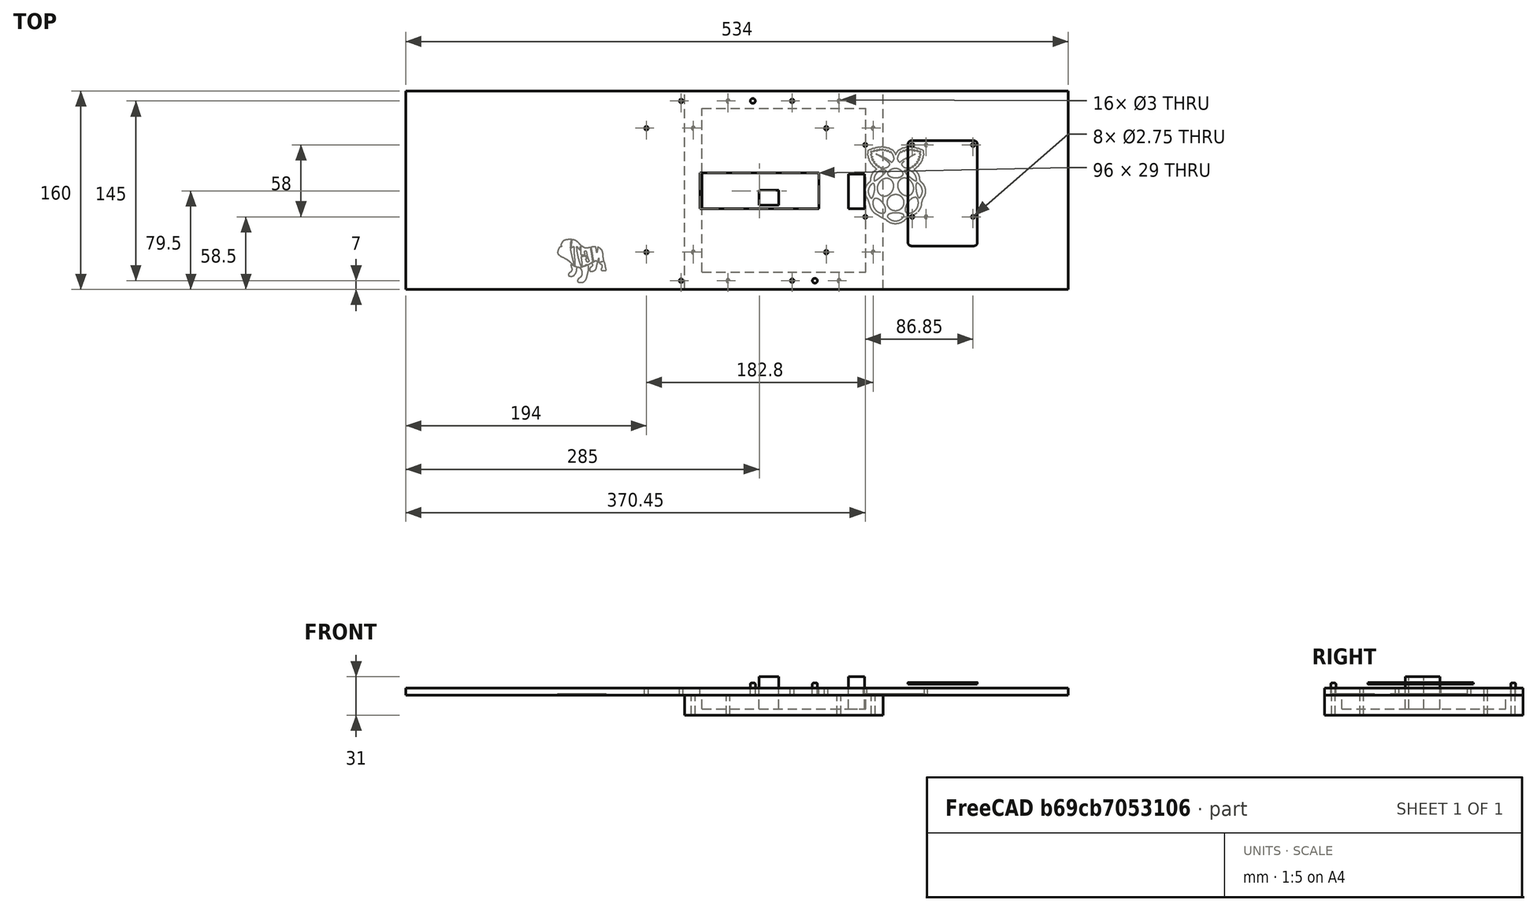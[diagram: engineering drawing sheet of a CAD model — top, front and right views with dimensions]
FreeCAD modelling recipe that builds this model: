
FCSTD DOCUMENT  (FreeCAD 0.19R)
Label: BigLEDWindowArray
License: All rights reserved
LicenseURL: http://en.wikipedia.org/wiki/All_rights_reserved
objects: Part::Feature×34, Part::Cylinder×26, Part::Extrusion×15, Part::Cut×10, Part::Box×9, Part::MultiFuse×9, Part::Fillet×3, Part::FeaturePython×2, TechDraw::DrawSVGTemplate×1, TechDraw::DrawViewPart×1, TechDraw::DrawPage×1
note: 108 computed .brp shape members not serialized (recipe doc carries the construction recipe); baked Part::Feature solids carry a one-line shape summary decoded from their .brp

FEATURE [Part::Box] Box  label="Cube"
  AttacherType = Attacher::AttachEngine3D
  Height = 16
  Length = 160
  Width = 160
FEATURE [Part::Cylinder] Cylinder
  Angle = 360
  AttacherType = Attacher::AttachEngine3D
  Height = 16
  Placement = pos=(35,7,0) rot=(0,0,1;0rad)
  Radius = 1.5
FEATURE [Part::Cylinder] Cylinder001
  Angle = 360
  AttacherType = Attacher::AttachEngine3D
  Height = 16
  Placement = pos=(124.5,7,0) rot=(0,0,1;0rad)
  Radius = 1.5
FEATURE [Part::Cylinder] Cylinder002
  Angle = 360
  AttacherType = Attacher::AttachEngine3D
  Height = 16
  Placement = pos=(35,152,0) rot=(0,0,1;0rad)
  Radius = 1.5
FEATURE [Part::Cylinder] Cylinder003
  Angle = 360
  AttacherType = Attacher::AttachEngine3D
  Height = 16
  Placement = pos=(124.5,152,0) rot=(0,0,1;0rad)
  Radius = 1.5
FEATURE [Part::Cylinder] Cylinder004
  Angle = 360
  AttacherType = Attacher::AttachEngine3D
  Height = 16
  Placement = pos=(7,30,0) rot=(0,0,1;0rad)
  Radius = 1.5
FEATURE [Part::Cylinder] Cylinder005
  Angle = 360
  AttacherType = Attacher::AttachEngine3D
  Height = 16
  Placement = pos=(7,130,0) rot=(0,0,1;0rad)
  Radius = 1.5
FEATURE [Part::Cylinder] Cylinder006
  Angle = 360
  AttacherType = Attacher::AttachEngine3D
  Height = 16
  Placement = pos=(152,30,0) rot=(0,0,1;0rad)
  Radius = 1.5
FEATURE [Part::Cylinder] Cylinder007
  Angle = 360
  AttacherType = Attacher::AttachEngine3D
  Height = 16
  Placement = pos=(152,130,0) rot=(0,0,1;0rad)
  Radius = 1.5
FEATURE [Part::MultiFuse] Fusion  label="Anchor Holes"
  Shapes = -> [Cylinder007,Cylinder,Cylinder001,Cylinder002,Cylinder003,Cylinder004,Cylinder005,Cylinder006]
FEATURE [Part::Box] Box001  label="Cube001"
  AttacherType = Attacher::AttachEngine3D
  Height = 11
  Length = 132
  Placement = pos=(14,14,5) rot=(0,0,1;0rad)
  Width = 132
FEATURE [Part::Cut] Cut
  Base = -> Box
  Tool = -> Box001
FEATURE [Part::Box] Box002  label="Cube002"
  AttacherType = Attacher::AttachEngine3D
  Height = 26
  Length = 16
  Placement = pos=(60,68,5) rot=(0,0,1;0rad)
  Width = 12
FEATURE [Part::Box] Box003  label="Cube003"
  AttacherType = Attacher::AttachEngine3D
  Height = 26
  Length = 13
  Placement = pos=(132,65,5) rot=(0,0,1;0rad)
  Width = 28
FEATURE [Part::Cut] Cut001
  Base = -> Cut
  Tool = -> Fusion
FEATURE [Part::MultiFuse] Fusion001
  Shapes = -> [Cut001,Box002,Box003]
FEATURE [Part::Cylinder] Cylinder008
  Angle = 360
  AttacherType = Attacher::AttachEngine3D
  Height = 10
  Placement = pos=(105,7,16) rot=(0,0,1;0rad)
  Radius = 2
FEATURE [Part::Cylinder] Cylinder009
  Angle = 360
  AttacherType = Attacher::AttachEngine3D
  Height = 10
  Placement = pos=(55,152,16) rot=(0,0,1;0rad)
  Radius = 2
FEATURE [Part::Fillet] Fillet
  Base = -> Cylinder009
  Edges = 1 edges r=1: [Edge1]
FEATURE [Part::Fillet] Fillet001
  Base = -> Cylinder008
  Edges = 1 edges r=1: [Edge1]
FEATURE [Part::MultiFuse] Fusion002  label="LED Array"
  Placement = pos=(224.8,0,-16) rot=(0,0,1;0rad)
  Shapes = -> [Fusion001,Fillet,Fillet001]
FEATURE [Part::Box] Box004  label="Plexiglass Base"
  AttacherType = Attacher::AttachEngine3D
  Height = 6
  Length = 609.6
  Width = 160
FEATURE [Part::Box] Box005  label="Main Cabling Hole"
  AttacherType = Attacher::AttachEngine3D
  Height = 6
  Length = 96
  Placement = pos=(274.8,65,0) rot=(0,0,1;0rad)
  Width = 29
FEATURE [Part::Box] Box006  label="Cube004"
  AttacherType = Attacher::AttachEngine3D
  Height = 1.4
  Length = 56
  Placement = pos=(0,0,9) rot=(0,0,1;0rad)
  Width = 85
FEATURE [Part::Fillet] Fillet002  label="Pi Base Board"
  Base = -> Box006
  Edges = 4 edges r=3: [Edge1,Edge3,Edge5,Edge7]
FEATURE [Part::Cylinder] Cylinder010
  Angle = 360
  AttacherType = Attacher::AttachEngine3D
  Height = 1.4
  Placement = pos=(3.5,81.5,9) rot=(0,0,1;0rad)
  Radius = 1.375
FEATURE [Part::Cylinder] Cylinder011
  Angle = 360
  AttacherType = Attacher::AttachEngine3D
  Height = 1.4
  Placement = pos=(52.5,81.5,9) rot=(0,0,1;0rad)
  Radius = 1.375
FEATURE [Part::Cylinder] Cylinder012
  Angle = 360
  AttacherType = Attacher::AttachEngine3D
  Height = 1.4
  Placement = pos=(52.5,23.5,9) rot=(0,0,1;0rad)
  Radius = 1.375
FEATURE [Part::Cylinder] Cylinder013
  Angle = 360
  AttacherType = Attacher::AttachEngine3D
  Height = 1.4
  Placement = pos=(3.5,23.5,9) rot=(0,0,1;0rad)
  Radius = 1.375
FEATURE [Part::MultiFuse] Fusion003  label="Pi Board Holes"
  Shapes = -> [Cylinder010,Cylinder011,Cylinder012,Cylinder013]
FEATURE [Part::Cut] Cut002  label="Pi base Board"
  Base = -> Fillet002
  Placement = pos=(404.8,35,0) rot=(0,0,1;0rad)
  Tool = -> Fusion003
FEATURE [Part::Cut] Cut003
  Base = -> Box004
  Tool = -> Box005
FEATURE [Part::Cylinder] Cylinder014
  Angle = 360
  AttacherType = Attacher::AttachEngine3D
  Height = 16
  Placement = pos=(35,152,0) rot=(0,0,1;0rad)
  Radius = 1.5
FEATURE [Part::Cylinder] Cylinder015
  Angle = 360
  AttacherType = Attacher::AttachEngine3D
  Height = 16
  Placement = pos=(152,130,0) rot=(0,0,1;0rad)
  Radius = 1.5
FEATURE [Part::Cylinder] Cylinder016
  Angle = 360
  AttacherType = Attacher::AttachEngine3D
  Height = 16
  Placement = pos=(124.5,7,0) rot=(0,0,1;0rad)
  Radius = 1.5
FEATURE [Part::Cylinder] Cylinder017
  Angle = 360
  AttacherType = Attacher::AttachEngine3D
  Height = 16
  Placement = pos=(7,30,0) rot=(0,0,1;0rad)
  Radius = 1.5
FEATURE [Part::Cylinder] Cylinder018
  Angle = 360
  AttacherType = Attacher::AttachEngine3D
  Height = 16
  Placement = pos=(7,130,0) rot=(0,0,1;0rad)
  Radius = 1.5
FEATURE [Part::Cylinder] Cylinder019
  Angle = 360
  AttacherType = Attacher::AttachEngine3D
  Height = 16
  Placement = pos=(152,30,0) rot=(0,0,1;0rad)
  Radius = 1.5
FEATURE [Part::Cylinder] Cylinder020
  Angle = 360
  AttacherType = Attacher::AttachEngine3D
  Height = 16
  Placement = pos=(124.5,152,0) rot=(0,0,1;0rad)
  Radius = 1.5
FEATURE [Part::Cylinder] Cylinder021
  Angle = 360
  AttacherType = Attacher::AttachEngine3D
  Height = 16
  Placement = pos=(35,7,0) rot=(0,0,1;0rad)
  Radius = 1.5
FEATURE [Part::MultiFuse] Fusion004  label="Anchor Holes001"
  Placement = pos=(224.8,0,-6) rot=(0,0,1;0rad)
  Shapes = -> [Cylinder015,Cylinder021,Cylinder016,Cylinder014,Cylinder020,Cylinder017,Cylinder018,Cylinder019]
FEATURE [Part::Cut] Cut004
  Base = -> Cut003
  Tool = -> Fusion004
FEATURE [Part::Cylinder] Cylinder022
  Angle = 360
  AttacherType = Attacher::AttachEngine3D
  Height = 6
  Placement = pos=(3.5,81.5,9) rot=(0,0,1;0rad)
  Radius = 1.375
FEATURE [Part::Cylinder] Cylinder023
  Angle = 360
  AttacherType = Attacher::AttachEngine3D
  Height = 6
  Placement = pos=(52.5,81.5,9) rot=(0,0,1;0rad)
  Radius = 1.375
FEATURE [Part::Cylinder] Cylinder024
  Angle = 360
  AttacherType = Attacher::AttachEngine3D
  Height = 6
  Placement = pos=(52.5,23.5,9) rot=(0,0,1;0rad)
  Radius = 1.375
FEATURE [Part::Cylinder] Cylinder025
  Angle = 360
  AttacherType = Attacher::AttachEngine3D
  Height = 6
  Placement = pos=(3.5,23.5,9) rot=(0,0,1;0rad)
  Radius = 1.375
FEATURE [Part::MultiFuse] Fusion005  label="Pi Board Holes001"
  Placement = pos=(404.75,35,-9) rot=(0,0,1;0rad)
  Shapes = -> [Cylinder022,Cylinder023,Cylinder024,Cylinder025]
FEATURE [Part::Cut] Cut005
  Base = -> Cut004
  Tool = -> Fusion005
FEATURE [Part::Feature] path94001
  shape: bbox 33.87 x 16.22 x 2e-07 mm, 1 faces, 0 solids (baked)
FEATURE [Part::Feature] path94003
  shape: bbox 26.79 x 32.02 x 2e-07 mm, 1 faces, 0 solids (baked)
FEATURE [Part::Feature] path94011
  shape: bbox 31.87 x 18.53 x 2e-07 mm, 1 faces, 0 solids (baked)
FEATURE [Part::Feature] path94013
  shape: bbox 47.72 x 38.86 x 2e-07 mm, 1 faces, 0 solids (baked)
FEATURE [Part::Feature] path94012
  shape: bbox 47.88 x 38.81 x 2e-07 mm, 1 faces, 0 solids (baked)
FEATURE [Part::Feature] path94009
  shape: bbox 25.13 x 21.74 x 2e-07 mm, 1 faces, 0 solids (baked)
FEATURE [Part::Feature] path94010
  shape: bbox 24.8 x 21.99 x 2e-07 mm, 1 faces, 0 solids (baked)
FEATURE [Part::Feature] path94007
  shape: bbox 33.34 x 35.47 x 2e-07 mm, 1 faces, 0 solids (baked)
FEATURE [Part::Feature] path94005
  shape: bbox 13.29 x 29.98 x 2e-07 mm, 1 faces, 0 solids (baked)
FEATURE [Part::Feature] path94004
  shape: bbox 34.84 x 32.78 x 2e-07 mm, 1 faces, 0 solids (baked)
FEATURE [Part::Feature] path94006
  shape: bbox 13.93 x 30.32 x 2e-07 mm, 1 faces, 0 solids (baked)
FEATURE [Part::Feature] path94008
  shape: bbox 32.64 x 35.5 x 2e-07 mm, 1 faces, 0 solids (baked)
FEATURE [Part::Feature] path94
  shape: bbox 121.7 x 156.1 x 2e-07 mm, 1 faces, 0 solids (baked)
FEATURE [Part::Feature] path94002
  shape: bbox 26 x 29.63 x 2e-07 mm, 1 faces, 0 solids (baked)
FEATURE [Part::Extrusion] Extrude001
  Base = -> path94001
  Dir = (0,0,1)
  DirMode = 0
  FaceMakerClass = Part::FaceMakerBullseye
  LengthFwd = 1
  LengthRev = 0
  Solid = false
  Symmetric = false
FEATURE [Part::Extrusion] Extrude
  Base = -> path94
  Dir = (0,0,1)
  DirMode = 0
  FaceMakerClass = Part::FaceMakerBullseye
  LengthFwd = 1
  LengthRev = 0
  Solid = false
  Symmetric = false
FEATURE [Part::Extrusion] Extrude012
  Base = -> path94012
  Dir = (0,0,1)
  DirMode = 0
  FaceMakerClass = Part::FaceMakerBullseye
  LengthFwd = 1
  LengthRev = 0
  Solid = false
  Symmetric = false
FEATURE [Part::Extrusion] Extrude013
  Base = -> path94013
  Dir = (0,0,1)
  DirMode = 0
  FaceMakerClass = Part::FaceMakerBullseye
  LengthFwd = 1
  LengthRev = 0
  Solid = false
  Symmetric = false
FEATURE [Part::Extrusion] Extrude007
  Base = -> path94007
  Dir = (0,0,1)
  DirMode = 0
  FaceMakerClass = Part::FaceMakerBullseye
  LengthFwd = 1
  LengthRev = 0
  Solid = false
  Symmetric = false
FEATURE [Part::Extrusion] Extrude008
  Base = -> path94008
  Dir = (0,0,1)
  DirMode = 0
  FaceMakerClass = Part::FaceMakerBullseye
  LengthFwd = 1
  LengthRev = 0
  Solid = false
  Symmetric = false
FEATURE [Part::Extrusion] Extrude009
  Base = -> path94009
  Dir = (0,0,1)
  DirMode = 0
  FaceMakerClass = Part::FaceMakerBullseye
  LengthFwd = 1
  LengthRev = 0
  Solid = false
  Symmetric = false
FEATURE [Part::Extrusion] Extrude010
  Base = -> path94010
  Dir = (0,0,1)
  DirMode = 0
  FaceMakerClass = Part::FaceMakerBullseye
  LengthFwd = 1
  LengthRev = 0
  Solid = false
  Symmetric = false
FEATURE [Part::Extrusion] Extrude011
  Base = -> path94011
  Dir = (0,0,1)
  DirMode = 0
  FaceMakerClass = Part::FaceMakerBullseye
  LengthFwd = 1
  LengthRev = 0
  Solid = false
  Symmetric = false
FEATURE [Part::Extrusion] Extrude002
  Base = -> path94002
  Dir = (0,0,1)
  DirMode = 0
  FaceMakerClass = Part::FaceMakerBullseye
  LengthFwd = 1
  LengthRev = 0
  Solid = false
  Symmetric = false
FEATURE [Part::Extrusion] Extrude003
  Base = -> path94003
  Dir = (0,0,1)
  DirMode = 0
  FaceMakerClass = Part::FaceMakerBullseye
  LengthFwd = 1
  LengthRev = 0
  Solid = false
  Symmetric = false
FEATURE [Part::Extrusion] Extrude004
  Base = -> path94004
  Dir = (0,0,1)
  DirMode = 0
  FaceMakerClass = Part::FaceMakerBullseye
  LengthFwd = 1
  LengthRev = 0
  Solid = false
  Symmetric = false
FEATURE [Part::Extrusion] Extrude005
  Base = -> path94005
  Dir = (0,0,1)
  DirMode = 0
  FaceMakerClass = Part::FaceMakerBullseye
  LengthFwd = 1
  LengthRev = 0
  Solid = false
  Symmetric = false
FEATURE [Part::Extrusion] Extrude006
  Base = -> path94006
  Dir = (0,0,1)
  DirMode = 0
  FaceMakerClass = Part::FaceMakerBullseye
  LengthFwd = 1
  LengthRev = 0
  Solid = false
  Symmetric = false
FEATURE [Part::MultiFuse] Fusion006
  Shapes = -> [Extrude001,Extrude002,Extrude003,Extrude004,Extrude005,Extrude006,Extrude007,Extrude008,Extrude009,Extrude010,Extrude011,Extrude012,Extrude013]
FEATURE [Part::Cut] Cut006  label="Pi Logo Base"
  Base = -> Extrude
  Tool = -> Fusion006
FEATURE [Part::FeaturePython] Clone  label="Pi Logo Scaled"  # Draft clone (typed FeaturePython)
  AttacherType = Attacher::AttachEngine3D
  Fuse = false
  Objects = -> [Cut006]
  Placement = pos=(408,115,0) rot=(0,0,1;0rad)
  Scale = (0.4,0.4,1)
FEATURE [Part::Cut] Cut007  label="Cut008"
  Base = -> Cut005
  Tool = -> Clone
FEATURE [Part::Feature] path821
  shape: bbox 45.55 x 68.49 x 2e-07 mm, 1 faces, 0 solids (baked)
FEATURE [Part::Feature] path821012
  shape: bbox 68.21 x 106 x 2e-07 mm, 1 faces, 0 solids (baked)
FEATURE [Part::Feature] path821018
  shape: bbox 52.44 x 63.16 x 2e-07 mm, 1 faces, 0 solids (baked)
FEATURE [Part::Feature] path821015
  shape: bbox 6.997 x 23.23 x 2e-07 mm, 1 faces, 0 solids (baked)
FEATURE [Part::Feature] path821019
  shape: bbox 51.27 x 62.42 x 2e-07 mm, 1 faces, 0 solids (baked)
FEATURE [Part::Feature] path821002
  shape: bbox 35.55 x 51.16 x 2e-07 mm, 1 faces, 0 solids (baked)
FEATURE [Part::Feature] path821009
  shape: bbox 42.61 x 110.8 x 2e-07 mm, 1 faces, 0 solids (baked)
FEATURE [Part::Feature] path821014
  shape: bbox 7.359 x 24.27 x 2e-07 mm, 1 faces, 0 solids (baked)
FEATURE [Part::Feature] path821017
  shape: bbox 6.224 x 14.06 x 2e-07 mm, 1 faces, 0 solids (baked)
FEATURE [Part::Feature] path821011
  shape: bbox 48.65 x 80.12 x 2e-07 mm, 1 faces, 0 solids (baked)
FEATURE [Part::Feature] path821007
  shape: bbox 26.33 x 36.96 x 2e-07 mm, 1 faces, 0 solids (baked)
FEATURE [Part::Feature] path821003
  shape: bbox 35.13 x 49.65 x 2e-07 mm, 1 faces, 0 solids (baked)
FEATURE [Part::Feature] path821008
  shape: bbox 43.59 x 111.6 x 2e-07 mm, 1 faces, 0 solids (baked)
FEATURE [Part::Feature] path821001
  shape: bbox 44.63 x 68.06 x 2e-07 mm, 1 faces, 0 solids (baked)
FEATURE [Part::Feature] path821013
  shape: bbox 67.42 x 105.1 x 2e-07 mm, 1 faces, 0 solids (baked)
FEATURE [Part::Feature] path821010
  shape: bbox 49.55 x 81.35 x 2e-07 mm, 1 faces, 0 solids (baked)
FEATURE [Part::Feature] path821004
  shape: bbox 33.13 x 41.25 x 2e-07 mm, 1 faces, 0 solids (baked)
FEATURE [Part::Feature] path821005
  shape: bbox 32.33 x 40.59 x 2e-07 mm, 1 faces, 0 solids (baked)
FEATURE [Part::Feature] path821006
  shape: bbox 26.59 x 37.55 x 2e-07 mm, 1 faces, 0 solids (baked)
FEATURE [Part::Feature] path821016
  shape: bbox 7.036 x 15.12 x 2e-07 mm, 1 faces, 0 solids (baked)
FEATURE [Part::MultiFuse] Fusion007
  Shapes = -> [path821,path821019,path821001,path821002,path821003,path821004,path821005,path821006,path821007,path821008,path821009,path821010,path821011,path821012,path821013,path821014,path821015,path821016,path821017,path821018]
FEATURE [Part::Extrusion] Extrude014  label="NGTBLogo"
  Base = -> Fusion007
  Dir = (0,0,1)
  DirMode = 0
  FaceMakerClass = Part::FaceMakerBullseye
  LengthFwd = 1
  LengthRev = 0
  Solid = false
  Symmetric = false
FEATURE [Part::FeaturePython] Clone001  label="NGTBLogo001"  # Draft clone (typed FeaturePython)
  AttacherType = Attacher::AttachEngine3D
  Fuse = false
  Objects = -> [Extrude014]
  Placement = pos=(200,41,1) rot=(0,1,0;3.14159rad)
  Scale = (0.2,0.2,1)
FEATURE [Part::Cut] Cut008  label="Cut009"
  Base = -> Cut007
  Tool = -> Clone001
FEATURE [Part::Box] Box007  label="Cube005"
  AttacherType = Attacher::AttachEngine3D
  Height = 6
  Length = 37.8
  Width = 160
FEATURE [Part::Box] Box008  label="Cube006"
  AttacherType = Attacher::AttachEngine3D
  Height = 6
  Length = 37.8
  Placement = pos=(571.8,0,0) rot=(0,0,1;0rad)
  Width = 160
FEATURE [Part::MultiFuse] Fusion008  label="Crop width blocks"
  Shapes = -> [Box008,Box007]
FEATURE [Part::Cut] Cut009  label="Cut010"
  Base = -> Cut008
  Placement = pos=(-37.8,0,0) rot=(0,0,1;0rad)
  Tool = -> Fusion008
FEATURE [TechDraw::DrawSVGTemplate] Template
  Height = 841
  Orientation = 1
  Width = 1189
FEATURE [TechDraw::DrawViewPart] View
  CoarseView = false
  Direction = (0,0,-1)
  Focus = 100
  HardHidden = false
  IsoCount = 0
  IsoHidden = false
  IsoVisible = false
  LockPosition = false
  Perspective = false
  Rotation = 0
  ScaleType = 0
  SeamHidden = false
  SeamVisible = true
  SmoothHidden = false
  SmoothVisible = true
  Source = -> [Cut009]
  X = 594.5
  XDirection = (-1,0,0)
  Y = 420.5
FEATURE [TechDraw::DrawPage] Page
  KeepUpdated = true
  NextBalloonIndex = 1
  ProjectionType = 0
  Template = -> Template
  Views = -> [View]
